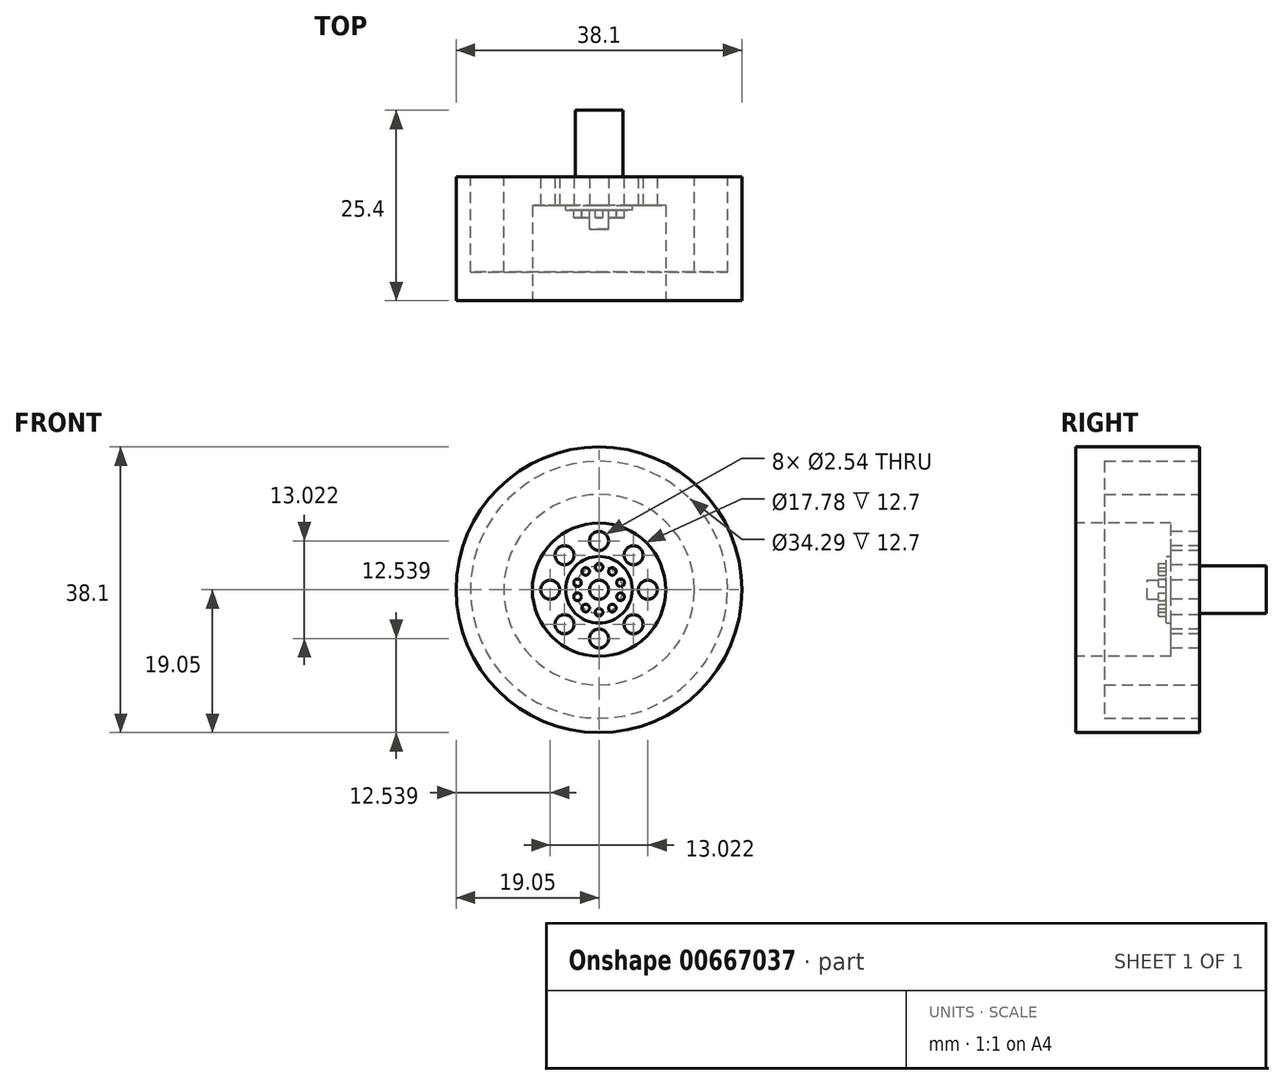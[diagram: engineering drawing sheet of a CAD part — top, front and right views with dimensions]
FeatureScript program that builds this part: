
annotation { "Feature Type Name" : "Feature", "Feature Type Description" : "" }
export const myFeature = defineFeature(function(context is Context, id is Id, definition is map)
    precondition{}
    {
        {
            var Q0;
            Q0=qCreatedBy(makeId("Front.planeOp"),FACE);
            var sketch = newSketch(context, id + "F0", { "sketchPlane" : qUnion([Q0])});
            skCircle(sketch, "E0", {"center": v(0, 0) * mm, "radius": 19.05 * mm});
            skSolve(sketch);
        }
        {
            var Q0;
            Q0=makeQuery(id+"F0.imprint","IMPRINT",FACE,{"disambiguationData":[TD([[makeQuery(id+"F0.imprint","IMPRINT",EDGE,{"derivedFrom":sQuery(id+"F0.wireOp",EDGE,"E0")}),1.0]])]});
            extrude(context, id + "F1", {"entities" : qUnion([Q0]), "oppositeDirection" : true, "depth" : 16.5 * mm, "offsetDistance" : 25.4 * mm});
        }
        {
            var Q0;
            Q0=makeQuery(id+"F1.opExtrude","CAP_FACE",FACE,{"disambiguationData":[OSD([sQuery(id+"F0.wireOp",EDGE,"E0")])],"isStart":true});
            var sketch = newSketch(context, id + "F2", { "sketchPlane" : qUnion([Q0])});
            skCircle(sketch, "E1", {"center": v(0, 0) * mm, "radius": 8.9 * mm});
            skSolve(sketch);
        }
        {
            var Q0;
            Q0=makeQuery(id+"F2.imprint","IMPRINT",FACE,{"disambiguationData":[TD([[makeQuery(id+"F2.imprint","IMPRINT",EDGE,{"derivedFrom":sQuery(id+"F2.wireOp",EDGE,"E1")}),1.0]])]});
            var sketch = newSketch(context, id + "F3", { "sketchPlane" : qUnion([Q0])});
            skCircle(sketch, "E2", {"center": v(0, 6.51) * mm, "radius": 1.27 * mm});
            skCircle(sketch, "E3.1.0", {"center": v(-4.6, 4.6) * mm, "radius": 1.27 * mm});
            skCircle(sketch, "E3.2.0", {"center": v(-6.51, 0) * mm, "radius": 1.27 * mm});
            skCircle(sketch, "E3.3.0", {"center": v(-4.6, -4.6) * mm, "radius": 1.27 * mm});
            skCircle(sketch, "E3.4.0", {"center": v(0, -6.51) * mm, "radius": 1.27 * mm});
            skCircle(sketch, "E3.5.0", {"center": v(4.6, -4.6) * mm, "radius": 1.27 * mm});
            skCircle(sketch, "E3.6.0", {"center": v(6.51, 0) * mm, "radius": 1.27 * mm});
            skCircle(sketch, "E3.7.0", {"center": v(4.6, 4.6) * mm, "radius": 1.27 * mm});
            skPoint(sketch, "E3.center", {"position": v(0, 0) * mm});
            skSolve(sketch);
        }
        {
            var Q0;
            Q0=makeQuery(id+"F2.imprint","IMPRINT",FACE,{"disambiguationData":[TD([[makeQuery(id+"F2.imprint","IMPRINT",EDGE,{"derivedFrom":sQuery(id+"F2.wireOp",EDGE,"E1")}),1.0]])]});
            extrude(context, id + "F4", {"entities" : qUnion([Q0]), "operationType" : NewBodyOperationType.REMOVE, "oppositeDirection" : true, "depth" : 12.7 * mm, "offsetDistance" : 25.4 * mm});
        }
        {
            var Q0;
            Q0=makeQuery(id+"F3.imprint","IMPRINT",FACE,{"disambiguationData":[TD([[makeQuery(id+"F3.imprint","IMPRINT",EDGE,{"derivedFrom":sQuery(id+"F3.wireOp",EDGE,"E2")}),1.0]])]});
            var Q1;
            Q1=makeQuery(id+"F3.imprint","IMPRINT",FACE,{"disambiguationData":[TD([[makeQuery(id+"F3.imprint","IMPRINT",EDGE,{"derivedFrom":sQuery(id+"F3.wireOp",EDGE,"E3.7.0")}),1.0]])]});
            var Q2;
            Q2=makeQuery(id+"F3.imprint","IMPRINT",FACE,{"disambiguationData":[TD([[makeQuery(id+"F3.imprint","IMPRINT",EDGE,{"derivedFrom":sQuery(id+"F3.wireOp",EDGE,"E3.6.0")}),1.0]])]});
            var Q3;
            Q3=makeQuery(id+"F3.imprint","IMPRINT",FACE,{"disambiguationData":[TD([[makeQuery(id+"F3.imprint","IMPRINT",EDGE,{"derivedFrom":sQuery(id+"F3.wireOp",EDGE,"E3.5.0")}),1.0]])]});
            var Q4;
            Q4=makeQuery(id+"F3.imprint","IMPRINT",FACE,{"disambiguationData":[TD([[makeQuery(id+"F3.imprint","IMPRINT",EDGE,{"derivedFrom":sQuery(id+"F3.wireOp",EDGE,"E3.4.0")}),1.0]])]});
            var Q5;
            Q5=makeQuery(id+"F3.imprint","IMPRINT",FACE,{"disambiguationData":[TD([[makeQuery(id+"F3.imprint","IMPRINT",EDGE,{"derivedFrom":sQuery(id+"F3.wireOp",EDGE,"E3.3.0")}),1.0]])]});
            var Q6;
            Q6=makeQuery(id+"F3.imprint","IMPRINT",FACE,{"disambiguationData":[TD([[makeQuery(id+"F3.imprint","IMPRINT",EDGE,{"derivedFrom":sQuery(id+"F3.wireOp",EDGE,"E3.2.0")}),1.0]])]});
            var Q7;
            Q7=makeQuery(id+"F3.imprint","IMPRINT",FACE,{"disambiguationData":[TD([[makeQuery(id+"F3.imprint","IMPRINT",EDGE,{"derivedFrom":sQuery(id+"F3.wireOp",EDGE,"E3.1.0")}),1.0]])]});
            extrude(context, id + "F5", {"entities" : qUnion([Q0, Q1, Q2, Q3, Q4, Q5, Q6, Q7]), "operationType" : NewBodyOperationType.REMOVE, "oppositeDirection" : true, "depth" : 25.4 * mm, "offsetDistance" : 25.4 * mm});
        }
        {
            var Q0;
            Q0=makeQuery(id+"F4.boolean.opBoolean","COPY",FACE,{"derivedFrom":makeQuery(id+"F4.opExtrude","CAP_FACE",FACE,{"disambiguationData":[OSD([sQuery(id+"F2.wireOp",EDGE,"E1")])],"isStart":false})});
            var sketch = newSketch(context, id + "F6", { "sketchPlane" : qUnion([Q0])});
            skCircle(sketch, "E4", {"center": v(0, 0) * mm, "radius": 3.18 * mm});
            skSolve(sketch);
        }
        {
            var Q0;
            Q0=makeQuery(id+"F6.imprint","IMPRINT",FACE,{"disambiguationData":[TD([[makeQuery(id+"F6.imprint","IMPRINT",EDGE,{"derivedFrom":sQuery(id+"F6.wireOp",EDGE,"E4")}),1.0]])]});
            extrude(context, id + "F7", {"entities" : qUnion([Q0]), "operationType" : NewBodyOperationType.ADD, "oppositeDirection" : true, "depth" : 12.7 * mm, "offsetDistance" : 25.4 * mm});
        }
        {
            var Q0;
            Q0=makeQuery(id+"F4.boolean.opBoolean","COPY",FACE,{"derivedFrom":makeQuery(id+"F4.opExtrude","CAP_FACE",FACE,{"disambiguationData":[OSD([sQuery(id+"F2.wireOp",EDGE,"E1")])],"isStart":false})});
            var sketch = newSketch(context, id + "F8", { "sketchPlane" : qUnion([Q0])});
            skCircle(sketch, "E5", {"center": v(0, 0) * mm, "radius": 4.45 * mm});
            skSolve(sketch);
        }
        {
            var Q0;
            Q0=makeQuery(id+"F8.imprint","IMPRINT",FACE,{"disambiguationData":[TD([[makeQuery(id+"F8.imprint","IMPRINT",EDGE,{"derivedFrom":sQuery(id+"F8.wireOp",EDGE,"E5")}),1.0]])]});
            extrude(context, id + "F9", {"entities" : qUnion([Q0]), "operationType" : NewBodyOperationType.ADD, "depth" : 0.64 * mm, "offsetDistance" : 25.4 * mm});
        }
        {
            var Q0;
            Q0=makeQuery(id+"F9.opExtrude","CAP_FACE",FACE,{"disambiguationData":[OSD([sQuery(id+"F8.wireOp",EDGE,"E5")])],"isStart":false});
            var sketch = newSketch(context, id + "F10", { "sketchPlane" : qUnion([Q0])});
            skCircle(sketch, "E6", {"center": v(0, 0) * mm, "radius": 1.27 * mm});
            skSolve(sketch);
        }
        {
            var Q0;
            Q0=makeQuery(id+"F10.imprint","IMPRINT",FACE,{"disambiguationData":[TD([[makeQuery(id+"F10.imprint","IMPRINT",EDGE,{"derivedFrom":sQuery(id+"F10.wireOp",EDGE,"E6")}),1.0]])]});
            extrude(context, id + "F11", {"entities" : qUnion([Q0]), "operationType" : NewBodyOperationType.ADD, "depth" : 2.54 * mm, "offsetDistance" : 25.4 * mm});
        }
        {
            var Q0;
            Q0=makeQuery(id+"F9.opExtrude","CAP_FACE",FACE,{"disambiguationData":[OSD([sQuery(id+"F8.wireOp",EDGE,"E5")])],"isStart":false});
            var sketch = newSketch(context, id + "F12", { "sketchPlane" : qUnion([Q0])});
            skCircle(sketch, "E7", {"center": v(0, 3.02) * mm, "radius": 0.5 * mm});
            skCircle(sketch, "E8.1.0", {"center": v(-1.77, 2.44) * mm, "radius": 0.5 * mm});
            skCircle(sketch, "E8.2.0", {"center": v(-2.87, 0.93) * mm, "radius": 0.5 * mm});
            skCircle(sketch, "E8.3.0", {"center": v(-2.87, -0.93) * mm, "radius": 0.5 * mm});
            skCircle(sketch, "E8.4.0", {"center": v(-1.77, -2.44) * mm, "radius": 0.5 * mm});
            skCircle(sketch, "E8.5.0", {"center": v(0, -3.02) * mm, "radius": 0.5 * mm});
            skCircle(sketch, "E8.6.0", {"center": v(1.77, -2.44) * mm, "radius": 0.5 * mm});
            skCircle(sketch, "E8.7.0", {"center": v(2.87, -0.93) * mm, "radius": 0.5 * mm});
            skCircle(sketch, "E8.8.0", {"center": v(2.87, 0.93) * mm, "radius": 0.5 * mm});
            skCircle(sketch, "E8.9.0", {"center": v(1.77, 2.44) * mm, "radius": 0.5 * mm});
            skPoint(sketch, "E8.center", {"position": v(0, 0) * mm});
            skSolve(sketch);
        }
        {
            var Q0;
            Q0=makeQuery(id+"F12.imprint","IMPRINT",FACE,{"disambiguationData":[TD([[makeQuery(id+"F12.imprint","IMPRINT",EDGE,{"derivedFrom":sQuery(id+"F12.wireOp",EDGE,"E8.9.0")}),1.0]])]});
            var Q1;
            Q1=makeQuery(id+"F12.imprint","IMPRINT",FACE,{"disambiguationData":[TD([[makeQuery(id+"F12.imprint","IMPRINT",EDGE,{"derivedFrom":sQuery(id+"F12.wireOp",EDGE,"E8.8.0")}),1.0]])]});
            var Q2;
            Q2=makeQuery(id+"F12.imprint","IMPRINT",FACE,{"disambiguationData":[TD([[makeQuery(id+"F12.imprint","IMPRINT",EDGE,{"derivedFrom":sQuery(id+"F12.wireOp",EDGE,"E8.7.0")}),1.0]])]});
            var Q3;
            Q3=makeQuery(id+"F12.imprint","IMPRINT",FACE,{"disambiguationData":[TD([[makeQuery(id+"F12.imprint","IMPRINT",EDGE,{"derivedFrom":sQuery(id+"F12.wireOp",EDGE,"E8.6.0")}),1.0]])]});
            var Q4;
            Q4=makeQuery(id+"F12.imprint","IMPRINT",FACE,{"disambiguationData":[TD([[makeQuery(id+"F12.imprint","IMPRINT",EDGE,{"derivedFrom":sQuery(id+"F12.wireOp",EDGE,"E8.5.0")}),1.0]])]});
            var Q5;
            Q5=makeQuery(id+"F12.imprint","IMPRINT",FACE,{"disambiguationData":[TD([[makeQuery(id+"F12.imprint","IMPRINT",EDGE,{"derivedFrom":sQuery(id+"F12.wireOp",EDGE,"E8.4.0")}),1.0]])]});
            var Q6;
            Q6=makeQuery(id+"F12.imprint","IMPRINT",FACE,{"disambiguationData":[TD([[makeQuery(id+"F12.imprint","IMPRINT",EDGE,{"derivedFrom":sQuery(id+"F12.wireOp",EDGE,"E8.3.0")}),1.0]])]});
            var Q7;
            Q7=makeQuery(id+"F12.imprint","IMPRINT",FACE,{"disambiguationData":[TD([[makeQuery(id+"F12.imprint","IMPRINT",EDGE,{"derivedFrom":sQuery(id+"F12.wireOp",EDGE,"E8.2.0")}),1.0]])]});
            var Q8;
            Q8=makeQuery(id+"F12.imprint","IMPRINT",FACE,{"disambiguationData":[TD([[makeQuery(id+"F12.imprint","IMPRINT",EDGE,{"derivedFrom":sQuery(id+"F12.wireOp",EDGE,"E8.1.0")}),1.0]])]});
            var Q9;
            Q9=makeQuery(id+"F12.imprint","IMPRINT",FACE,{"disambiguationData":[TD([[makeQuery(id+"F12.imprint","IMPRINT",EDGE,{"derivedFrom":sQuery(id+"F12.wireOp",EDGE,"E7")}),1.0]])]});
            extrude(context, id + "F13", {"entities" : qUnion([Q0, Q1, Q2, Q3, Q4, Q5, Q6, Q7, Q8, Q9]), "operationType" : NewBodyOperationType.ADD, "depth" : 1.02 * mm, "offsetDistance" : 25.4 * mm});
        }
        {
            var Q0;
            Q0=makeQuery(id+"F1.opExtrude","CAP_FACE",FACE,{"disambiguationData":[OSD([sQuery(id+"F0.wireOp",EDGE,"E0")])],"isStart":false});
            var sketch = newSketch(context, id + "F14", { "sketchPlane" : qUnion([Q0])});
            skCircle(sketch, "E9", {"center": v(0, 0) * mm, "radius": 12.7 * mm});
            skCircle(sketch, "E10", {"center": v(0, 0) * mm, "radius": 17.15 * mm});
            skSolve(sketch);
        }
        {
            var Q0;
            Q0=makeQuery(id+"F14.imprint","IMPRINT",FACE,{"disambiguationData":[TD([[makeQuery(id+"F14.imprint","IMPRINT",EDGE,{"derivedFrom":sQuery(id+"F14.wireOp",EDGE,"E9")}),-1.0]])]});
            extrude(context, id + "F15", {"entities" : qUnion([Q0]), "operationType" : NewBodyOperationType.REMOVE, "oppositeDirection" : true, "depth" : 12.7 * mm, "offsetDistance" : 25.4 * mm});
        }
    });
